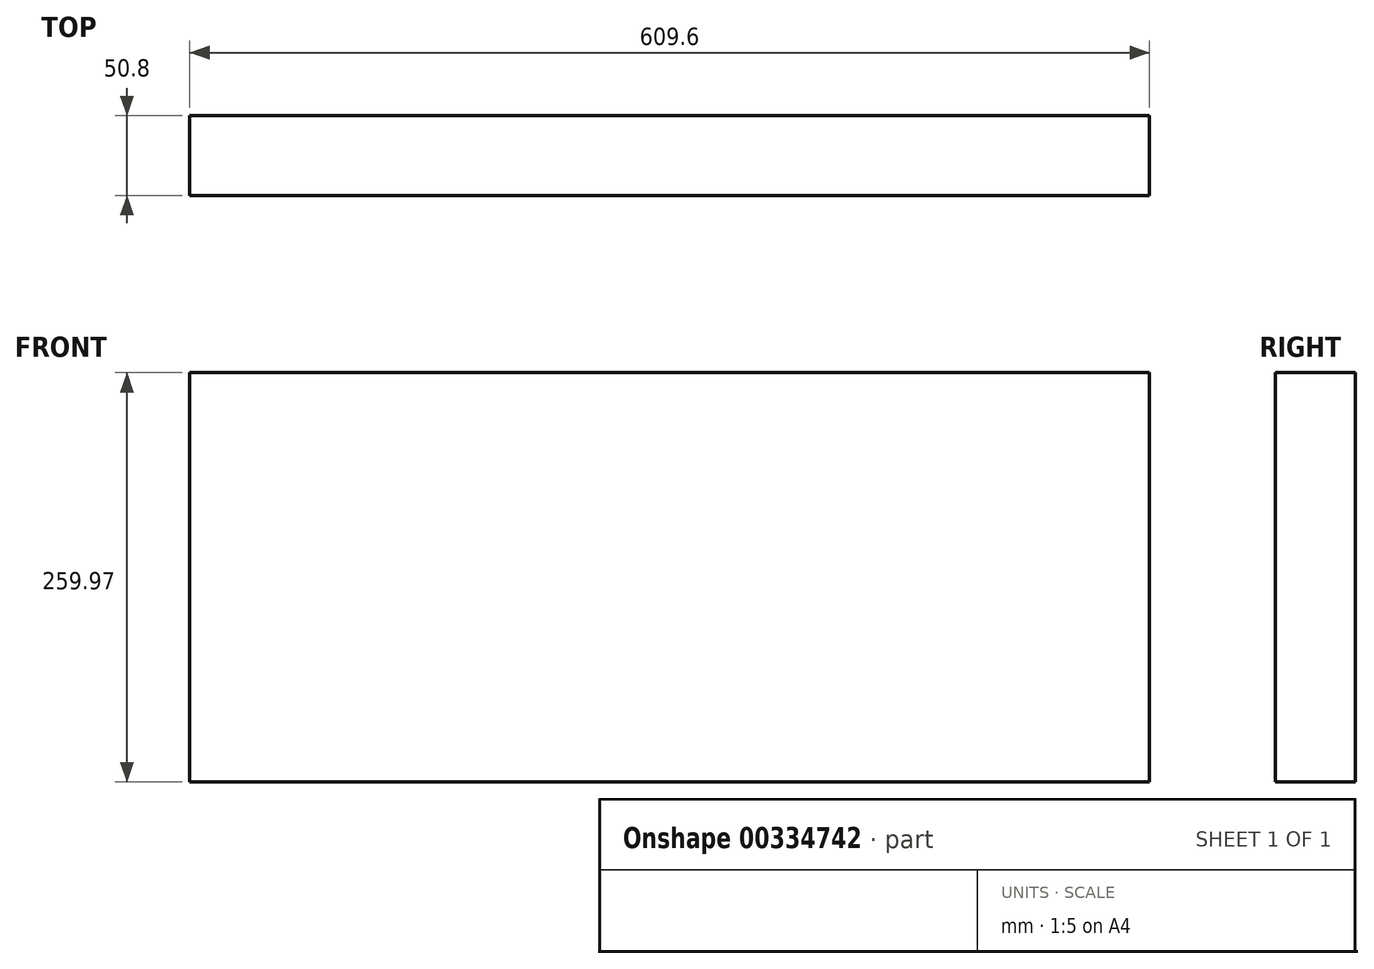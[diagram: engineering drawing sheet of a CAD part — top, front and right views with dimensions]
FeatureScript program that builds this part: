
annotation { "Feature Type Name" : "Feature", "Feature Type Description" : "" }
export const myFeature = defineFeature(function(context is Context, id is Id, definition is map)
    precondition{}
    {
        {
            var Q0;
            Q0=qCreatedBy(makeId("Front.planeOp"),FACE);
            var sketch = newSketch(context, id + "F0", { "sketchPlane" : qUnion([Q0])});
            skLineSegment(sketch, "E0.bottom", {"start": v(-315.71, 155.26) * mm, "end": v(293.89, 155.26) * mm});
            skLineSegment(sketch, "E0.top", {"start": v(-315.71, -104.71) * mm, "end": v(293.89, -104.71) * mm});
            skLineSegment(sketch, "E0.left", {"start": v(-315.71, 155.26) * mm, "end": v(-315.71, -104.71) * mm});
            skLineSegment(sketch, "E0.right", {"start": v(293.89, 155.26) * mm, "end": v(293.89, -104.71) * mm});
            skSolve(sketch);
        }
        {
            var Q0;
            Q0 = qSketchRegion(id + "F0", true);
            extrude(context, id + "F1", {"entities" : qUnion([Q0]), "depth" : 50.8 * mm});
        }
    });
